# Revit family: Strangregulierventil mit Messventilen für Trinkwasseranlagen 4217 GNW
name_source: partatom
category: Rohrzubehör
units: mm (PartAtom-declared; Revit-internal decimal feet)

## family parameters
Arbeitsebenenbasiert = Nein
Beim Laden mit Abzugskörper schneiden = Nein
Bemaßung runder Anschluss = Durchmesser verwenden
Gemeinsam genutzt = Nein
Immer vertikal = Ja
OmniClass-Nummer = 23.65.55.14
OmniClass-Titel = Valves for Liquid Services
Teiletyp = Unterbricht

## types (1)
- Strangregulierventil mit Messventilen für Trinkwasseranlagen 4217 GNW
    Anwendungen = Zum Absperren und Regulieren von Trinkwasseranlagen in Gebäuden bzw. zum hydraulischen Abgleich von Versorgungsleitungen.
    Ausführung = STRÖMAX-GNW Strangregulierventil mit Messventilen, 1/2′′ – 2′′, mit gleichprozentiger Kennlinie.
Geradesitzform, gelbe Ausführung, Muffe x Muffe, nichtsteigende Spindel, Spindelabdichtung mit Doppel-O-Ring, Voreinstellung durch Hubbegrenzung mittels Innenspindel, Anzeige der Voreinstellstufe am Handradschaft.
2 Messventile sind neben dem Handrad montiert.
    D04 = 16.25 mm  [stored 0.0533136 ft]
    D05 = 16.75 mm
    Differenzdruckmessung = STRÖMAX-GNW Strangregulierventil ist mit zwei Messventilen ausgestattet.
Bei Verwendung eines geeigneten Messgerätes kann der Differenzdruck gemessen und dadurch die jeweilige Durchflussmenge in Abhängigkeit der Einstellstufe ermittelt werden.
Am HERZ-Messcomputer (1 8900 05) ist außerdem direkt die jeweilige Durchflussmenge ablesbar (siehe Gerätehandbuch).
    Einbaulage = Bedingt durch die senkrecht zur Ventilachse angeordnete, nichtsteigende Ventilspindel ist für jede Einbaulage optimale Zugängigkeit und Bedienbarkeit des Ventils gewährleistet.
    Gehäuse = Messing CW725N
    H01 = 41.5 mm  [stored 0.136155 ft]
    Handrad = Polyamid, grün
    Hersteller = HERZ Armaturen Ges.m.b.H.
    Innengewinde = gem. ISO 7/1
    MD01 = 7.4 mm  [stored 0.0242782 ft]
    Max. Betriebsdruck = 2500000.0 Pa
    Max. Betriebstemperatur = 85 °C
    Medium = Trinkwasser
    S02 = 60 mm  [stored 0.19685 ft]
    SCTWCODE = 04;00;02
    SCTWSEQ = FW;SBT_TYP_FW="109";2
    SC_NennweiteBerechnet = 0
    Spindel = Messing CW725N
    Spindelabdichtung = Doppel-O-Ring aus EPDM
    URL = www.herz-armaturen.at
    Vorgabe-Ansicht = 0 mm  [stored 0 ft]
    W01 = 30.00°
    W02 = 60.00°

note: [stored X ft] marks values corroborated as IEEE doubles in the binary element streams (Revit-internal decimal feet)
